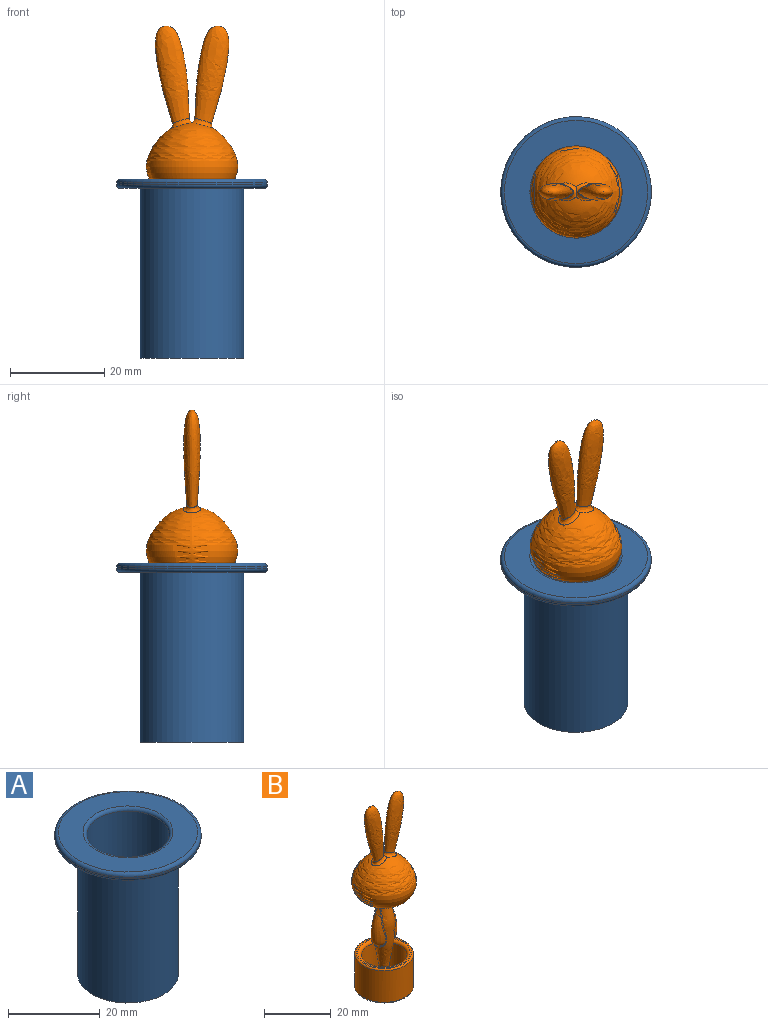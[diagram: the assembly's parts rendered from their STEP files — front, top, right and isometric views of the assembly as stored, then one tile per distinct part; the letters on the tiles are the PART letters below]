
ASSEMBLY  parts=2 mates=1
PART A: 10 faces, bbox 34.6x34.6x38 mm
  f0: plane 22x22mm, normal (0,0,-1), area 380.1mm2, adj f1
  f1: cylinder r=11mm len=36mm, axis (0,0,-1), area 2488.1mm2, adj f0,f2
  f2: plane 30.4x30.4mm, normal (0,0,-1), area 345.7mm2, adj f1,f3
  f3: torus R=15.2mm, axis (0,0,-1), area 124mm2, adj f2,f4
  f4: cylinder r=16mm len=32mm, axis (0,0,-1), area 40.2mm2, adj f3,f5
  f5: torus R=15.2mm, axis (0,0,-1), area 124mm2, adj f4,f6
  f6: plane 30.4x30.4mm, normal (0,0,1), area 424.1mm2, adj f5,f7
  f7: torus R=9.8mm, axis (0,0,-1), area 73.4mm2, adj f6,f8
  f8: cylinder r=9mm len=35.2mm, axis (0,0,-1), area 1990.5mm2, adj f7,f9
  f9: plane 18x18mm, normal (0,0,1), area 254.5mm2, adj f8
PART B: 17 faces, bbox 19.3x19.3x68.9 mm
  f0: revolved ~45.93x19.34mm, area 1319.5mm2, adj f1,f8,f9,f12,f13
  f1: plane 13.6x13.6mm, normal (0,0,1), area 140mm2, adj f0,f2
  f2: cylinder r=6.8mm len=13.6mm, axis (0,0,-1), area 405.9mm2, adj f1,f14
  f3: plane 16.6x16.6mm, normal (0,0,1), area 25.3mm2, adj f14,f15
  f4: cylinder r=8.8mm len=17.6mm, axis (0,0,-1), area 635.9mm2, adj f15,f16
  f5: plane 16.6x16.6mm, normal (0,0,-1), area 216.4mm2, adj f16
  f6: bspline ~16.95x11.56mm, area 71.6mm2, adj f9
  f7: bspline ~13.1x5.16mm, area 72.8mm2, adj f8
  f8: bspline ~14.07x5.37mm, area 13mm2, adj f0,f7
  f9: bspline ~14.07x5.37mm, area 13mm2, adj f0,f6
  f10: bspline ~23.17x7.92mm, area 264.8mm2, adj f12
  f11: bspline ~23.17x7.92mm, area 265.4mm2, adj f13
  f12: bspline ~4.98x3.82mm, area 15mm2, adj f0,f10,f13
  f13: bspline ~4.97x3.81mm, area 15.1mm2, adj f0,f11,f12
  f14: torus R=7.8mm, axis (0,0,-1), area 70.7mm2, adj f2,f3
  f15: torus R=8.3mm, axis (0,0,-1), area 42.5mm2, adj f3,f4
  f16: torus R=8.3mm, axis (0,0,1), area 42.5mm2, adj f4,f5
PLACE A at identity fixed
PLACE B at identity
MATE slider B.f2 <-> A.f1  axis (0,0,-1) through (0,0,0)mm
